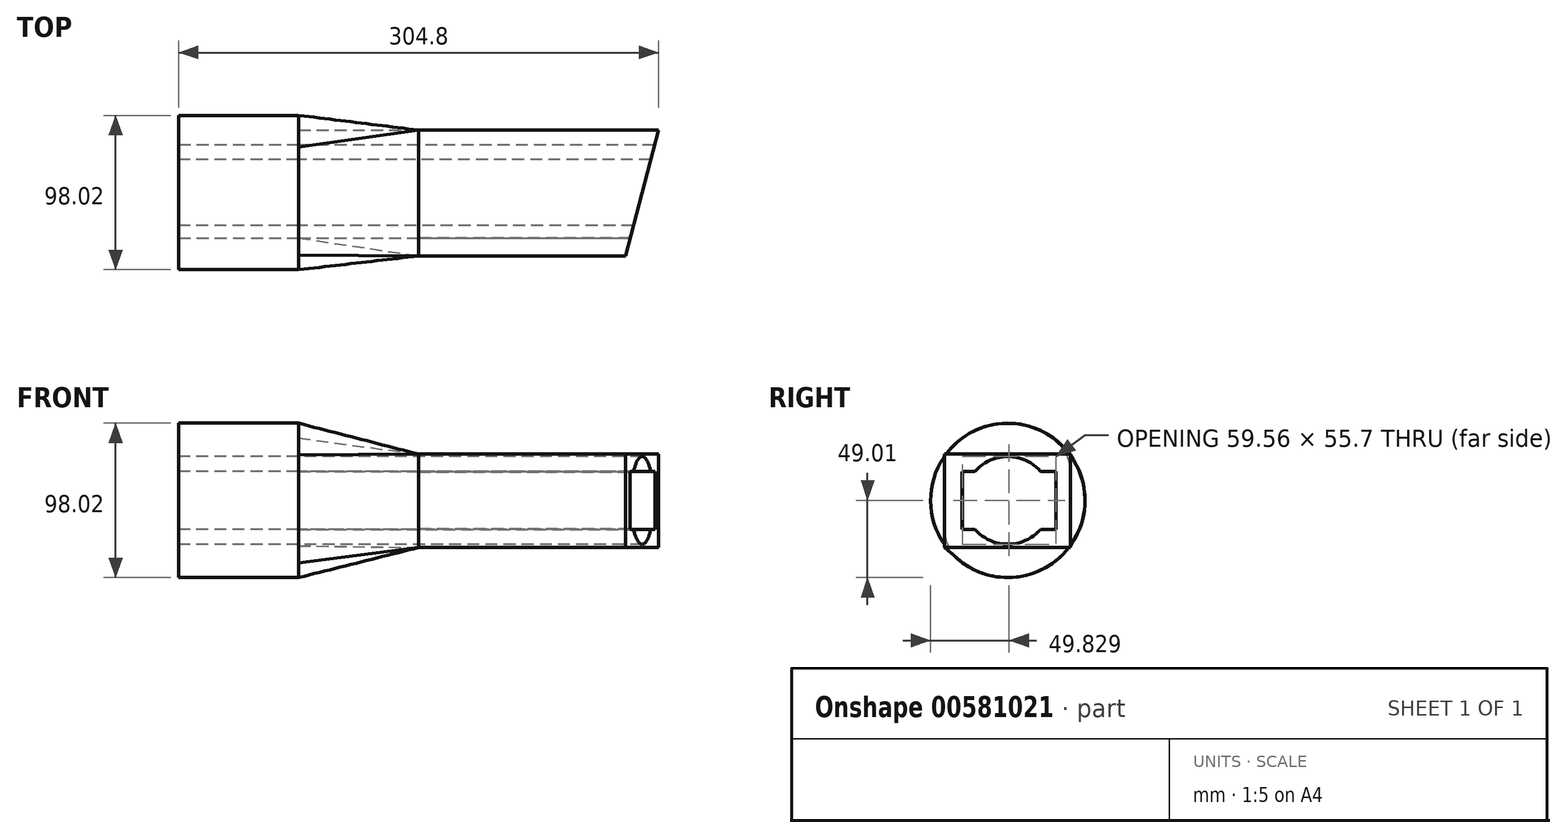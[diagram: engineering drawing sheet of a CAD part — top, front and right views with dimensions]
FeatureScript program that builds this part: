
annotation { "Feature Type Name" : "Feature", "Feature Type Description" : "" }
export const myFeature = defineFeature(function(context is Context, id is Id, definition is map)
    precondition{}
    {
        {
            var Q0;
            Q0=qCreatedBy(makeId("Right.planeOp"),FACE);
            var sketch = newSketch(context, id + "F0", { "sketchPlane" : qUnion([Q0])});
            skCircle(sketch, "E0", {"center": v(0, 0) * mm, "radius": 49.01 * mm});
            skSolve(sketch);
        }
        {
            var Q0;
            Q0=makeQuery(id+"F0.imprint","IMPRINT",FACE,{"disambiguationData":[TD([[makeQuery(id+"F0.imprint","IMPRINT",EDGE,{"derivedFrom":sQuery(id+"F0.wireOp",EDGE,"E0")}),1.0]])]});
            extrude(context, id + "F1", {"entities" : qUnion([Q0]), "depth" : 76.2 * mm, "offsetDistance" : 25.4 * mm});
        }
        {
            var Q0;
            Q0=makeQuery(id+"F1.opExtrude","CAP_FACE",FACE,{"disambiguationData":[OSD([sQuery(id+"F0.wireOp",EDGE,"E0")])],"isStart":false});
            cPlane(context, id + "F2", {"entities" : qUnion([Q0]), "cplaneType" : CPlaneType.OFFSET, "offset" : 76.2 * mm, "width" : 152.4 * mm, "height" : 152.4 * mm});
        }
        {
            var Q0;
            Q0=qCreatedBy(id+"F2.planeOp",FACE);
            var sketch = newSketch(context, id + "F3", { "sketchPlane" : qUnion([Q0])});
            skLineSegment(sketch, "E1.bottom", {"start": v(-40.27, 29.35) * mm, "end": v(39.65, 29.35) * mm});
            skLineSegment(sketch, "E1.top", {"start": v(-40.27, -29.97) * mm, "end": v(39.65, -29.97) * mm});
            skLineSegment(sketch, "E1.left", {"start": v(-40.27, 29.35) * mm, "end": v(-40.27, -29.97) * mm});
            skLineSegment(sketch, "E1.right", {"start": v(39.65, 29.35) * mm, "end": v(39.65, -29.97) * mm});
            skSolve(sketch);
        }
        {
            var Q0;
            Q0=makeQuery(id+"F1.opExtrude","CAP_FACE",FACE,{"disambiguationData":[OSD([sQuery(id+"F0.wireOp",EDGE,"E0")])],"isStart":false});
            var Q1;
            Q1=makeQuery(id+"F3.imprint","IMPRINT",FACE,{"disambiguationData":[TD([[makeQuery(id+"F3.imprint","IMPRINT",EDGE,{"derivedFrom":sQuery(id+"F3.wireOp",EDGE,"E1.bottom")}),-1.0]])]});
            loft(context, id + "F4", {"sheetProfilesArray" : [{ "sheetProfileEntities" : qUnion([Q0]) }, { "sheetProfileEntities" : qUnion([Q1]) }]});
        }
        {
            var Q0;
            Q0=makeQuery(id+"F4.opLoft","CAP_FACE",FACE,{"disambiguationData":[OSD([makeQuery(id+"F3.imprint","IMPRINT",FACE,{"disambiguationData":[TD([[makeQuery(id+"F3.imprint","IMPRINT",EDGE,{"derivedFrom":sQuery(id+"F3.wireOp",EDGE,"E1.bottom")}),-1.0]])]})])],"isStart":true});
            extrude(context, id + "F5", {"entities" : qUnion([Q0]), "operationType" : NewBodyOperationType.ADD, "depth" : 152.4 * mm, "offsetDistance" : 25.4 * mm});
        }
        {
            var Q0;
            Q0=makeQuery(id+"F5.opExtrude","SWEPT_FACE",FACE,{"disambiguationData":[OSD([sQuery(id+"F3.wireOp",EDGE,"E1.bottom"),sQuery(id+"F3.wireOp",EDGE,"E1.left"),sQuery(id+"F3.wireOp",EDGE,"E1.right")])]});
            var sketch = newSketch(context, id + "F6", { "sketchPlane" : qUnion([Q0])});
            skLineSegment(sketch, "E2", {"start": v(304.8, 39.65) * mm, "end": v(304.8, -40.27) * mm});
            skLineSegment(sketch, "E3", {"start": v(304.8, -40.27) * mm, "end": v(283.81, -40.27) * mm});
            skLineSegment(sketch, "E4", {"start": v(283.81, -40.27) * mm, "end": v(304.8, 39.65) * mm});
            skSolve(sketch);
        }
        {
            var Q0;
            Q0=makeQuery(id+"F6.imprint","IMPRINT",FACE,{"disambiguationData":[TD([[makeQuery(id+"F6.imprint","IMPRINT",EDGE,{"derivedFrom":sQuery(id+"F6.wireOp",EDGE,"E2")}),-1.0]])]});
            extrude(context, id + "F7", {"entities" : qUnion([Q0]), "operationType" : NewBodyOperationType.REMOVE, "endBound" : BoundingType.UP_TO_NEXT, "oppositeDirection" : true, "depth" : 25.4 * mm, "offsetDistance" : 25.4 * mm});
        }
        {
            var Q0;
            Q0=qCreatedBy(id+"F2.planeOp",FACE);
            cPlane(context, id + "F8", {"entities" : qUnion([Q0]), "cplaneType" : CPlaneType.OFFSET, "offset" : 152.4 * mm, "width" : 152.4 * mm, "height" : 152.4 * mm});
        }
        {
            var Q0;
            Q0=qCreatedBy(id+"F8.planeOp",FACE);
            var sketch = newSketch(context, id + "F9", { "sketchPlane" : qUnion([Q0])});
            skLineSegment(sketch, "E5.bottom", {"start": v(-29.03, 18.1) * mm, "end": v(30.28, 18.1) * mm});
            skLineSegment(sketch, "E5.top", {"start": v(-29.03, -18.1) * mm, "end": v(30.28, -18.1) * mm});
            skLineSegment(sketch, "E5.left", {"start": v(-29.03, 18.1) * mm, "end": v(-29.03, -18.1) * mm});
            skLineSegment(sketch, "E5.right", {"start": v(30.28, 18.1) * mm, "end": v(30.28, -18.1) * mm});
            skSolve(sketch);
        }
        {
            var Q0;
            Q0=makeQuery(id+"F9.imprint","IMPRINT",FACE,{"disambiguationData":[TD([[makeQuery(id+"F9.imprint","IMPRINT",EDGE,{"derivedFrom":sQuery(id+"F9.wireOp",EDGE,"E5.bottom")}),-1.0]])]});
            extrude(context, id + "F10", {"entities" : qUnion([Q0]), "operationType" : NewBodyOperationType.REMOVE, "oppositeDirection" : true, "depth" : 152.4 * mm, "offsetDistance" : 25.4 * mm});
        }
        {
            var Q0;
            Q0=makeQuery(id+"F1.opExtrude","CAP_FACE",FACE,{"disambiguationData":[OSD([sQuery(id+"F0.wireOp",EDGE,"E0")])],"isStart":true});
            var sketch = newSketch(context, id + "F11", { "sketchPlane" : qUnion([Q0])});
            skCircle(sketch, "E6", {"center": v(0, 0) * mm, "radius": 27.85 * mm});
            skSolve(sketch);
        }
        {
            var Q0;
            Q0=makeQuery(id+"F11.imprint","IMPRINT",FACE,{"disambiguationData":[TD([[makeQuery(id+"F11.imprint","IMPRINT",EDGE,{"derivedFrom":sQuery(id+"F11.wireOp",EDGE,"E6")}),1.0]])]});
            extrude(context, id + "F12", {"entities" : qUnion([Q0]), "operationType" : NewBodyOperationType.REMOVE, "endBound" : BoundingType.UP_TO_NEXT, "oppositeDirection" : true, "depth" : 25.4 * mm, "offsetDistance" : 25.4 * mm});
        }
        {
            var Q0;
            Q0=makeQuery(id+"F1.opExtrude","CAP_FACE",FACE,{"disambiguationData":[OSD([sQuery(id+"F0.wireOp",EDGE,"E0")])],"isStart":true});
            var sketch = newSketch(context, id + "F13", { "sketchPlane" : qUnion([Q0])});
            skCircle(sketch, "E7", {"center": v(0, 0) * mm, "radius": 27.85 * mm});
            skSolve(sketch);
        }
        {
            var Q0;
            Q0 = qSketchRegion(id + "F13", true);
            extrude(context, id + "F14", {"entities" : qUnion([Q0]), "operationType" : NewBodyOperationType.REMOVE, "oppositeDirection" : true, "depth" : 381 * mm, "offsetDistance" : 25.4 * mm});
        }
        {
            var Q0;
            Q0=qCreatedBy(id+"F8.planeOp",FACE);
            var sketch = newSketch(context, id + "F15", { "sketchPlane" : qUnion([Q0])});
            skLineSegment(sketch, "E8.bottom", {"start": v(30.6, 18.49) * mm, "end": v(-28.96, 18.49) * mm});
            skLineSegment(sketch, "E8.top", {"start": v(30.6, -18.39) * mm, "end": v(-28.96, -18.39) * mm});
            skLineSegment(sketch, "E8.left", {"start": v(30.6, 18.49) * mm, "end": v(30.6, -18.39) * mm});
            skLineSegment(sketch, "E8.right", {"start": v(-28.96, 18.49) * mm, "end": v(-28.96, -18.39) * mm});
            skSolve(sketch);
        }
        {
            var Q0;
            Q0 = qSketchRegion(id + "F15", true);
            extrude(context, id + "F16", {"entities" : qUnion([Q0]), "operationType" : NewBodyOperationType.REMOVE, "oppositeDirection" : true, "depth" : 381 * mm, "offsetDistance" : 25.4 * mm});
        }
    });
